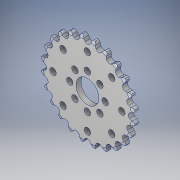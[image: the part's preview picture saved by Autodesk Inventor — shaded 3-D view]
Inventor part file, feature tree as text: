
AUTODESK INVENTOR PART (.ipt)
format: ipt  version: 2017 (Build 210142000, 142)  size: 418,816 bytes
history: native  units: in
note: dims shown in document units (in); Inventor stores cm internally (conversion verified against a paired STEP export)
features: plane x1, pattern_circular x1
ambient origin geometry x8: Origin, YZ Plane, XZ Plane, XY Plane, X Axis, Y Axis, Z Axis, Center Point
bodies: Solid1 (feature_tree)
feature tree (2):
  plane  "Work Plane1"
  pattern_circular  "CirPattern2"
